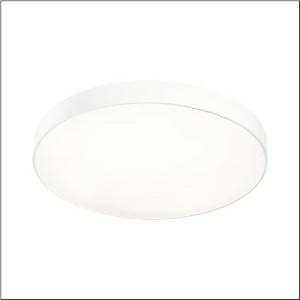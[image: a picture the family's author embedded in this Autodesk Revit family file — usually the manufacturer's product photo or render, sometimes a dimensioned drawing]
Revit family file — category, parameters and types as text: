
# Revit family: round_21_l_51mr38fd0421w
name_source: partatom
category: Lighting Fixtures
units: mm (PartAtom-declared; Revit-internal decimal feet)

## family parameters
Cut with Voids When Loaded = No
Host = Face
Light Source = No
Part Type = Normal
Room Calculation Point = No
Round Connector Dimension = Use Diameter
Shared = No

## types (1)
- Round 21 L (1 x LED, 14150 lm, 97 W, 4000K)
    Apparent Load = 97 VA
    CIE Flux Codes = 49 80 96 100 100
    Color Rendering = 80
    Color Temperature = 4000K
    Default Elevation = 1800 mm
    Description = Round 21 L, wall and ceiling luminaire, primary optical cover: cover, of PMMA, opal, light emission: direct distribution, primary light characteristic: symmetric, installation type: suspended mounting, surface-mounted, LED, rated luminous flux: 13.080lm, luminous efficacy: 146lm/W, light colour: 840, colour temperature: 4000K, control gear: DALI 2, with terminal, 5-pole, mains connection: 230V, AC, 50/60Hz, rated input power: 97W, housing, of aluminium, coated, white, diameter: 850mm, height: 62mm, protection rating (complete): IP40, insulation class (complete): insulation class I (protective earthing), certification: CE, impact resistance: IK04, permissible operating ambient temperature: -10..+35°C, packaging unit: 1 piece
    Height = 87 mm
    Lamp = 1 x LED
    Lamp Light Flux = 14150 lm
    Lamp Power = 97 W
    Lamp count = 1
    Length = 850 mm
    Luminous efficacy = 146 lm/W
    Manufacturer = Siteco
    ModVariant = No
    Model = 51MR38FD0421W
    Mounting Place = Ceiling
    Mounting Type = Surface mounted
    Number of Poles = 1
    OnlyDefault = Yes
    Power Factor = 1
    Product Name = Round 21 L
    Product group = wall and ceiling luminaire
    ProductGroupID = 304
    Protection Class = Protection class I
    Protection Degree = IP 40
    RLX_Detail_Level = 1
    RLX_Emergency_Light_Flux = 0 lm
    RLX_Emergency_Type = 0
    RLX_Emergency_Type_DB = No
    RlxData = <blob elided: 15013 chars, md5=3ad1cf6e>
    Socket = socket
    Standby Power = 0 W
    System Light Flux = 14150 lm
    System Power = 97 W
    Type Comments = Product without accessories
    Type Image = l_1258320.jpg
    URL = http://relux.com
    VarID = ---
    Voltage = 0 V
    Weight = 0.00 kg
    Width = 0 mm  [stored 0 ft]

note: [stored X ft] marks values corroborated as IEEE doubles in the binary element streams (Revit-internal decimal feet)

## geometry (parser evidence)
native form markers: Sweep x12
no freeform markers — native parametric forms only
